# Revit family: 501112171_Sanitario kiddy Ecoflush bicolor
name_source: partatom
category: Generic Models
units: mm (PartAtom-declared; Revit-internal decimal feet)

## family parameters
Always vertical = Yes
Can host rebar = No
Cut with Voids When Loaded = No
Part Type = Normal
Room Calculation Point = No
Round Connector Dimension = Use Diameter
Shared = No
Work Plane-Based = No

## types (1)
- 501112171_Sanitario kiddy Ecoflush bicolor
    CERAMIC COLOR = <By Category>
    Consumo de agua = 4.8 lpf (1,28 gpf)
    Description = Para facilitar el uso infantil, contamos con este sanitario cómodo, ergonómico y funcional, con asiento sanitario de cierre suave, tornillo de fijación que asegura la tapa al tanque y botón superior con diseño moderno. ¡Pídelo ahora!
    Dimensiones generales producto (H * W * D) = 573mm x 579mm x 293mm
    Garantía = Garantía ilimitada de por vida para la Porcelana
    Material = Corona_Porcelana_Sanitaria_Blanco
    Material 2 = Corona_Porcelana_Sanitaria_Azul
    Material 3 = Corona_Plastico_Rojo
    Sistema de descarga = Anillo abierto
    URL = https://corona.co

## geometry (parser evidence)
native form markers: Sweep x4
no freeform markers — native parametric forms only
